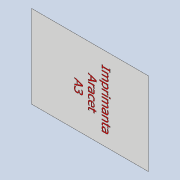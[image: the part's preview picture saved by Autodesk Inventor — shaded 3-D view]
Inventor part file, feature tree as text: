
AUTODESK INVENTOR PART (.ipt)
format: ipt  version: 2020 (Build 240168000, 168)  size: 589,312 bytes
history: native  units: mm
features: extrude x2, sketch x2
ambient origin geometry x8: Origin, YZ Plane, XZ Plane, XY Plane, X Axis, Y Axis, Z Axis, Center Point
bodies: Solid1 (feature_tree)
feature tree (4):
  extrude  "Extrusion1"  Depth=297.0mm
  extrude  "Extrusion2"  Depth=0.01mm TaperAngle=0.0deg
  sketch  "Sketch1"  dims[d0=420.0mm d1=297.0mm]
  sketch  "Sketch2"  dims[d2=0.15mm d3=0.0mm d4=0.01mm d5=0.0mm]
